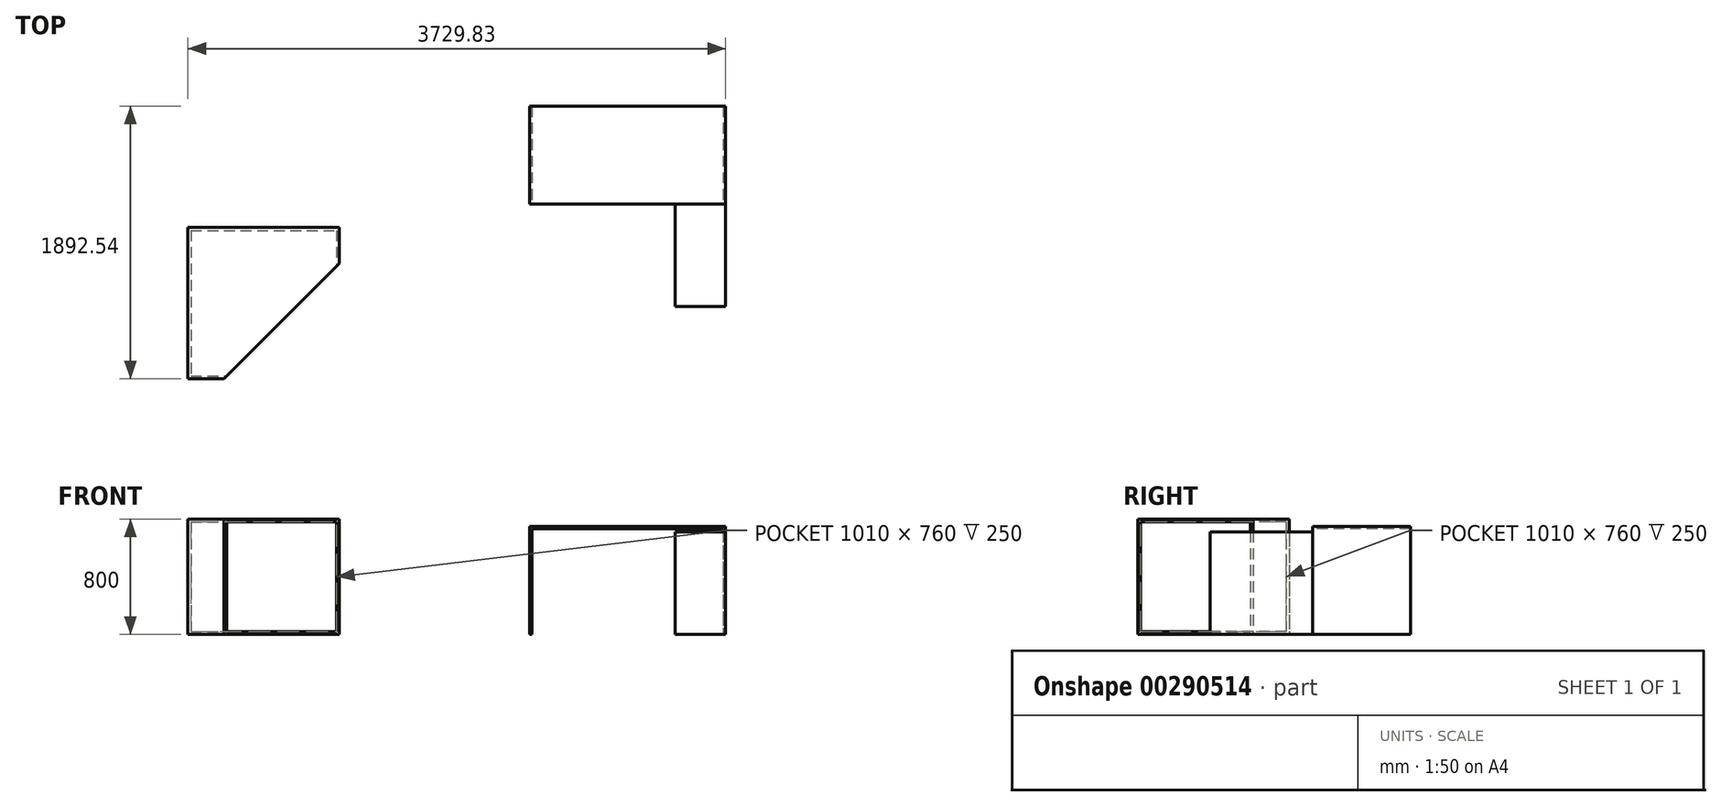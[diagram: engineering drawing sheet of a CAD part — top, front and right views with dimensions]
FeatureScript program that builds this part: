
annotation { "Feature Type Name" : "Feature", "Feature Type Description" : "" }
export const myFeature = defineFeature(function(context is Context, id is Id, definition is map)
    precondition{}
    {
        {
            var Q0;
            Q0=qCreatedBy(makeId("Top.planeOp"),FACE);
            var sketch = newSketch(context, id + "F0", { "sketchPlane" : qUnion([Q0])});
            skLineSegment(sketch, "E0.bottom", {"start": v(-115.6, 453.37) * mm, "end": v(1244.4, 453.37) * mm});
            skLineSegment(sketch, "E0.top", {"start": v(-115.6, -226.63) * mm, "end": v(1244.4, -226.63) * mm});
            skLineSegment(sketch, "E0.left", {"start": v(-115.6, 453.37) * mm, "end": v(-115.6, -226.63) * mm});
            skLineSegment(sketch, "E0.right", {"start": v(1244.4, 453.37) * mm, "end": v(1244.4, -226.63) * mm});
            skLineSegment(sketch, "E1.bottom", {"start": v(1244.4, 453.37) * mm, "end": v(894.4, 453.37) * mm});
            skLineSegment(sketch, "E1.top", {"start": v(1244.4, -936.63) * mm, "end": v(894.4, -936.63) * mm});
            skLineSegment(sketch, "E1.left", {"start": v(1244.4, 453.37) * mm, "end": v(1244.4, -936.63) * mm});
            skLineSegment(sketch, "E1.right", {"start": v(894.4, 453.37) * mm, "end": v(894.4, -936.63) * mm});
            skSolve(sketch);
        }
        {
            var Q0;
            {var subQ0=sQuery(id+"F0.wireOp",EDGE,"E0.bottom");Q0=makeQuery(id+"F0.imprint","IMPRINT",FACE,{"disambiguationData":[TD([[makeQuery(id+"F0.imprint","IMPRINT",EDGE,{"derivedFrom":subQ0}),-1.0]])]});}
            var Q1;
            {var subQ5=sQuery(id+"F0.wireOp",EDGE,"E1.bottom");Q1=makeQuery(id+"F0.imprint","IMPRINT",FACE,{"disambiguationData":[TD([[makeQuery(id+"F0.imprint","IMPRINT",EDGE,{"derivedFrom":subQ5}),1.0]])]});}
            extrude(context, id + "F1", {"entities" : qUnion([Q0, Q1]), "depth" : 750 * mm});
        }
        {
            var Q0;
            Q0=makeQuery(id+"F1.opExtrude","SWEPT_FACE",FACE,{"disambiguationData":[OSD([sQuery(id+"F0.wireOp",EDGE,"E0.top")])]});
            var Q1;
            Q1=makeQuery(id+"F1.opExtrude","SWEPT_FACE",FACE,{"disambiguationData":[OSD([sQuery(id+"F0.wireOp",EDGE,"E1.left")])]});
            var Q2;
            Q2=makeQuery(id+"F1.opExtrude","SWEPT_FACE",FACE,{"disambiguationData":[OSD([sQuery(id+"F0.wireOp",EDGE,"E0.bottom"),sQuery(id+"F0.wireOp",EDGE,"E1.bottom")])]});
            var Q3;
            Q3=makeQuery(id+"F1.opExtrude","CAP_FACE",FACE,{"disambiguationData":[OSD([sQuery(id+"F0.wireOp",EDGE,"E0.bottom"),sQuery(id+"F0.wireOp",EDGE,"E0.top"),sQuery(id+"F0.wireOp",EDGE,"E0.left"),sQuery(id+"F0.wireOp",EDGE,"E1.bottom"),sQuery(id+"F0.wireOp",EDGE,"E1.left")])],"isStart":true});
            shell(context, id + "F2", {"entities" : qUnion([Q0, Q1, Q2, Q3]), "thickness" : 15 * mm});
        }
        {
            var Q0;
            {var subQ5=sQuery(id+"F0.wireOp",EDGE,"E1.bottom");Q0=makeQuery(id+"F0.imprint","IMPRINT",FACE,{"disambiguationData":[TD([[makeQuery(id+"F0.imprint","IMPRINT",EDGE,{"derivedFrom":subQ5}),1.0]])]});}
            var Q1;
            {var subQ5=sQuery(id+"F0.wireOp",EDGE,"E1.top");Q1=makeQuery(id+"F0.imprint","IMPRINT",FACE,{"disambiguationData":[TD([[makeQuery(id+"F0.imprint","IMPRINT",EDGE,{"derivedFrom":subQ5}),-1.0]])]});}
            extrude(context, id + "F3", {"entities" : qUnion([Q0, Q1]), "depth" : 712 * mm});
        }
        {
            var Q0;
            {var subQ0=sQuery(id+"F0.wireOp",EDGE,"E0.bottom");Q0=makeQuery(id+"F0.imprint","IMPRINT",FACE,{"disambiguationData":[TD([[makeQuery(id+"F0.imprint","IMPRINT",EDGE,{"derivedFrom":subQ0}),-1.0]])]});}
            var sketch = newSketch(context, id + "F4", { "sketchPlane" : qUnion([Q0])});
            skLineSegment(sketch, "E2.bottom", {"start": v(-2485.43, -389.17) * mm, "end": v(-1435.43, -389.17) * mm});
            skLineSegment(sketch, "E2.top", {"start": v(-2485.43, -1439.17) * mm, "end": v(-2235.43, -1439.17) * mm});
            skLineSegment(sketch, "E2.left", {"start": v(-2485.43, -389.17) * mm, "end": v(-2485.43, -1439.17) * mm});
            skLineSegment(sketch, "E2.right", {"start": v(-1435.43, -389.17) * mm, "end": v(-1435.43, -639.17) * mm});
            skLineSegment(sketch, "E3", {"start": v(-2235.43, -1439.17) * mm, "end": v(-1435.43, -639.17) * mm});
            skSolve(sketch);
        }
        {
            var Q0;
            Q0=makeQuery(id+"F4.imprint","IMPRINT",FACE,{"disambiguationData":[TD([[makeQuery(id+"F4.imprint","IMPRINT",EDGE,{"derivedFrom":sQuery(id+"F4.wireOp",EDGE,"E2.bottom")}),-1.0]])]});
            extrude(context, id + "F5", {"entities" : qUnion([Q0]), "depth" : 800 * mm});
        }
        {
            var Q0;
            Q0=makeQuery(id+"F5.opExtrude","SWEPT_FACE",FACE,{"disambiguationData":[OSD([sQuery(id+"F4.wireOp",EDGE,"E3")])]});
            shell(context, id + "F6", {"entities" : qUnion([Q0]), "thickness" : 20 * mm});
        }
    });
